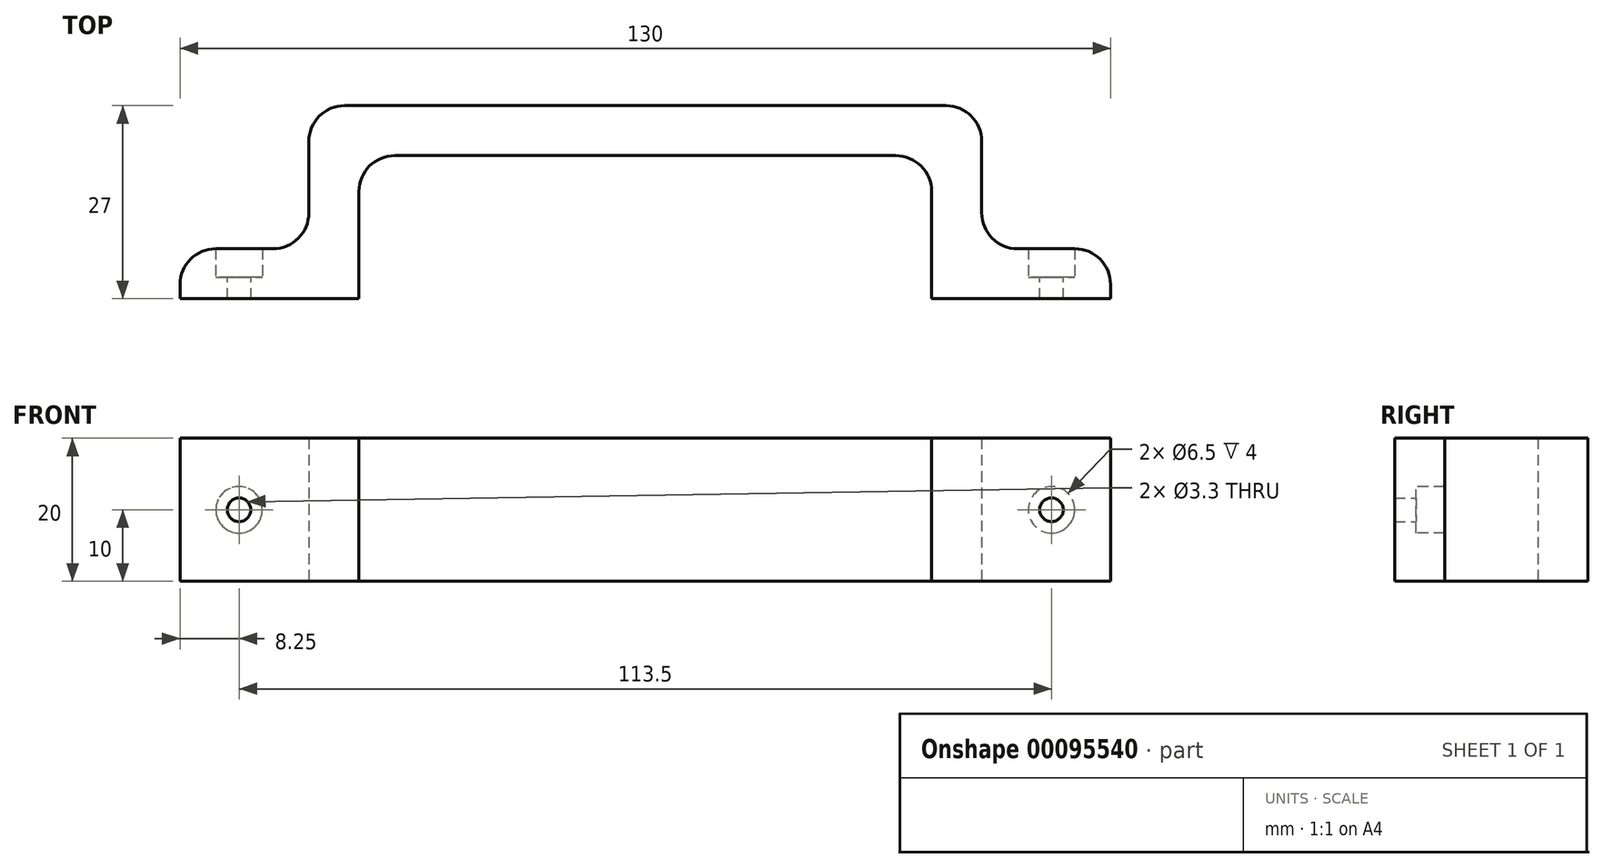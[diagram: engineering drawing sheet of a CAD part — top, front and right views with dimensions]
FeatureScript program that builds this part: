
annotation { "Feature Type Name" : "Feature", "Feature Type Description" : "" }
export const myFeature = defineFeature(function(context is Context, id is Id, definition is map)
    precondition{}
    {
        {
            var Q0;
            Q0=qCreatedBy(makeId("Top.planeOp"),FACE);
            var sketch = newSketch(context, id + "F0", { "sketchPlane" : qUnion([Q0])});
            skLineSegment(sketch, "E0", {"start": v(0, 20) * mm, "end": v(-40, 20) * mm});
            skLineSegment(sketch, "E1", {"start": v(-40, 20) * mm, "end": v(-40, 0) * mm});
            skLineSegment(sketch, "E2", {"start": v(-40, 0) * mm, "end": v(-65, 0) * mm});
            skLineSegment(sketch, "E3.0", {"start": v(-47, 7) * mm, "end": v(-65, 7) * mm});
            skLineSegment(sketch, "E3.1", {"start": v(-47, 27) * mm, "end": v(-47, 7) * mm});
            skLineSegment(sketch, "E3.2", {"start": v(0, 27) * mm, "end": v(-47, 27) * mm});
            skLineSegment(sketch, "E4", {"start": v(-65, 7) * mm, "end": v(-65, 0) * mm});
            skLineSegment(sketch, "E5.MirrorCS", {"start": v(40, 0) * mm, "end": v(65, 0) * mm});
            skLineSegment(sketch, "E6.MirrorCS", {"start": v(65, 7) * mm, "end": v(65, 0) * mm});
            skLineSegment(sketch, "E7.MirrorCS", {"start": v(40, 20) * mm, "end": v(40, 0) * mm});
            skLineSegment(sketch, "E8.MirrorCS", {"start": v(47, 7) * mm, "end": v(65, 7) * mm});
            skLineSegment(sketch, "E9.MirrorCS", {"start": v(0, 20) * mm, "end": v(40, 20) * mm});
            skLineSegment(sketch, "E10.MirrorCS", {"start": v(47, 27) * mm, "end": v(47, 7) * mm});
            skLineSegment(sketch, "E11.MirrorCS", {"start": v(0, 27) * mm, "end": v(47, 27) * mm});
            skSolve(sketch);
        }
        {
            var Q0;
            Q0 = qSketchRegion(id + "F0", true);
            extrude(context, id + "F1", {"entities" : qUnion([Q0]), "depth" : 20 * mm});
        }
        {
            var Q0;
            Q0=makeQuery(id+"F1.opExtrude","SWEPT_EDGE",EDGE,{"disambiguationData":[OSD([sQuery(id+"F0.wireOp",EDGE,"E7.MirrorCS"),sQuery(id+"F0.wireOp",EDGE,"E9.MirrorCS")])]});
            var Q1;
            Q1=makeQuery(id+"F1.opExtrude","SWEPT_EDGE",EDGE,{"disambiguationData":[OSD([sQuery(id+"F0.wireOp",EDGE,"E10.MirrorCS"),sQuery(id+"F0.wireOp",EDGE,"E11.MirrorCS")])]});
            var Q2;
            Q2=makeQuery(id+"F1.opExtrude","SWEPT_EDGE",EDGE,{"disambiguationData":[OSD([sQuery(id+"F0.wireOp",EDGE,"E0"),sQuery(id+"F0.wireOp",EDGE,"E1")])]});
            var Q3;
            Q3=makeQuery(id+"F1.opExtrude","SWEPT_EDGE",EDGE,{"disambiguationData":[OSD([sQuery(id+"F0.wireOp",EDGE,"E3.1"),sQuery(id+"F0.wireOp",EDGE,"E3.2")])]});
            var Q4;
            Q4=makeQuery(id+"F1.opExtrude","SWEPT_EDGE",EDGE,{"disambiguationData":[OSD([sQuery(id+"F0.wireOp",EDGE,"E8.MirrorCS"),sQuery(id+"F0.wireOp",EDGE,"E10.MirrorCS")])]});
            var Q5;
            Q5=makeQuery(id+"F1.opExtrude","SWEPT_EDGE",EDGE,{"disambiguationData":[OSD([sQuery(id+"F0.wireOp",EDGE,"E3.0"),sQuery(id+"F0.wireOp",EDGE,"E3.1")])]});
            var Q6;
            Q6=makeQuery(id+"F1.opExtrude","SWEPT_EDGE",EDGE,{"disambiguationData":[OSD([sQuery(id+"F0.wireOp",EDGE,"E6.MirrorCS"),sQuery(id+"F0.wireOp",EDGE,"E8.MirrorCS")])]});
            var Q7;
            Q7=makeQuery(id+"F1.opExtrude","SWEPT_EDGE",EDGE,{"disambiguationData":[OSD([sQuery(id+"F0.wireOp",EDGE,"E3.0"),sQuery(id+"F0.wireOp",EDGE,"E4")])]});
            fillet(context, id + "F2", {"entities" : qUnion([Q0, Q1, Q2, Q3, Q4, Q5, Q6, Q7]), "radius" : 5 * mm, "tangentPropagation" : true, "allowEdgeOverflow" : false});
        }
        {
            var Q0;
            Q0=makeQuery(id+"F1.opExtrude","SWEPT_FACE",FACE,{"disambiguationData":[OSD([sQuery(id+"F0.wireOp",EDGE,"E5.MirrorCS")])]});
            cPlane(context, id + "F3", {"entities" : qUnion([Q0]), "cplaneType" : CPlaneType.OFFSET, "offset" : 3 * mm, "oppositeDirection" : true, "width" : 150 * mm, "height" : 150 * mm});
        }
        {
            var Q0;
            Q0=qCreatedBy(id+"F3.planeOp",FACE);
            var sketch = newSketch(context, id + "F4", { "sketchPlane" : qUnion([Q0])});
            skCircle(sketch, "E12", {"center": v(-56.75, 10) * mm, "radius": 3.25 * mm});
            skPoint(sketch, "E13", {"position": v(-65, 10) * mm});
            skCircle(sketch, "E14.MirrorC", {"center": v(56.75, 10) * mm, "radius": 3.25 * mm});
            skSolve(sketch);
        }
        {
            var Q0;
            Q0 = qSketchRegion(id + "F4", true);
            extrude(context, id + "F5", {"entities" : qUnion([Q0]), "operationType" : NewBodyOperationType.REMOVE, "oppositeDirection" : true, "depth" : 25 * mm});
        }
        {
            var Q0;
            Q0=makeQuery(id+"F5.boolean.opBoolean","COPY",FACE,{"derivedFrom":makeQuery(id+"F5.opExtrude","CAP_FACE",FACE,{"disambiguationData":[OSD([sQuery(id+"F4.wireOp",EDGE,"E14.MirrorC")])],"isStart":true})});
            var sketch = newSketch(context, id + "F6", { "sketchPlane" : qUnion([Q0])});
            skCircle(sketch, "E15", {"center": v(-56.75, 10) * mm, "radius": 1.65 * mm});
            skCircle(sketch, "E16.MirrorC", {"center": v(56.75, 10) * mm, "radius": 1.65 * mm});
            skSolve(sketch);
        }
        {
            var Q0;
            Q0 = qSketchRegion(id + "F6", true);
            extrude(context, id + "F7", {"entities" : qUnion([Q0]), "operationType" : NewBodyOperationType.REMOVE, "oppositeDirection" : true, "depth" : 25 * mm});
        }
    });
